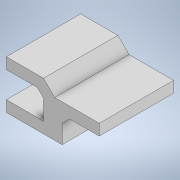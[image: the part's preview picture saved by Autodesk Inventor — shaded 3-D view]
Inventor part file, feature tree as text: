
AUTODESK INVENTOR PART (.ipt)
format: ipt  version: 2020 (Build 240168000, 168)  size: 142,336 bytes
history: native  units: mm
features: extrude x3, sketch x3, projected_geometry x2, other x1, chamfer x1
ambient origin geometry x8: Origin, YZ Plane, XZ Plane, XY Plane, X Axis, Y Axis, Z Axis, Center Point
bodies: Body1 (feature_tree)
feature tree (10):
  other  "Твердое тело1"
  extrude  "Выдавливание1"  Depth=5.0mm
  extrude  "Выдавливание2"  Depth=20.0mm
  chamfer  "Фаска1"  Distance=7.0mm
  extrude  "Выдавливание3"  Depth=10.0mm
  sketch  "Эскиз1"
  sketch  "Эскиз2"
  projected_geometry  "Спроецированная петля1"
  sketch  "Эскиз3"
  projected_geometry  "Спроецированная петля2"
